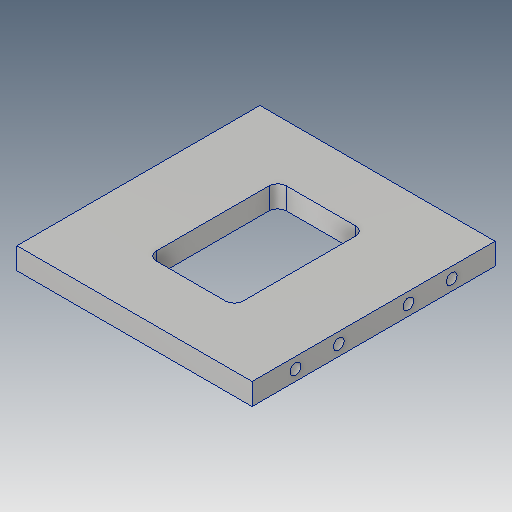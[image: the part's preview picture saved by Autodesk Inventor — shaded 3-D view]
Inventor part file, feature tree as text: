
AUTODESK INVENTOR PART (.ipt)
format: ipt  version: 2020.5 (Build 245400000, 400)  size: 144,384 bytes
history: native  units: mm
features: extrude x4, sketch x4, projected_geometry x2, other x1, fillet x1
ambient origin geometry x8: Origin, YZ Plane, XZ Plane, XY Plane, X Axis, Y Axis, Z Axis, Center Point
bodies: Body1 (feature_tree)
feature tree (12):
  other  "솔리드1"
  extrude  "돌출1"  Depth=54.2mm
  extrude  "돌출5"  Depth=56.0mm
  extrude  "돌출6"  Depth=27.1mm
  extrude  "돌출7"  Depth=28.0mm
  fillet  "모깎기1"  Radius=5.0mm
  sketch  "스케치1"
  sketch  "스케치5"
  projected_geometry  "투영된 루프3"
  sketch  "스케치6"
  projected_geometry  "투영된 루프4"
  sketch  "스케치7"
